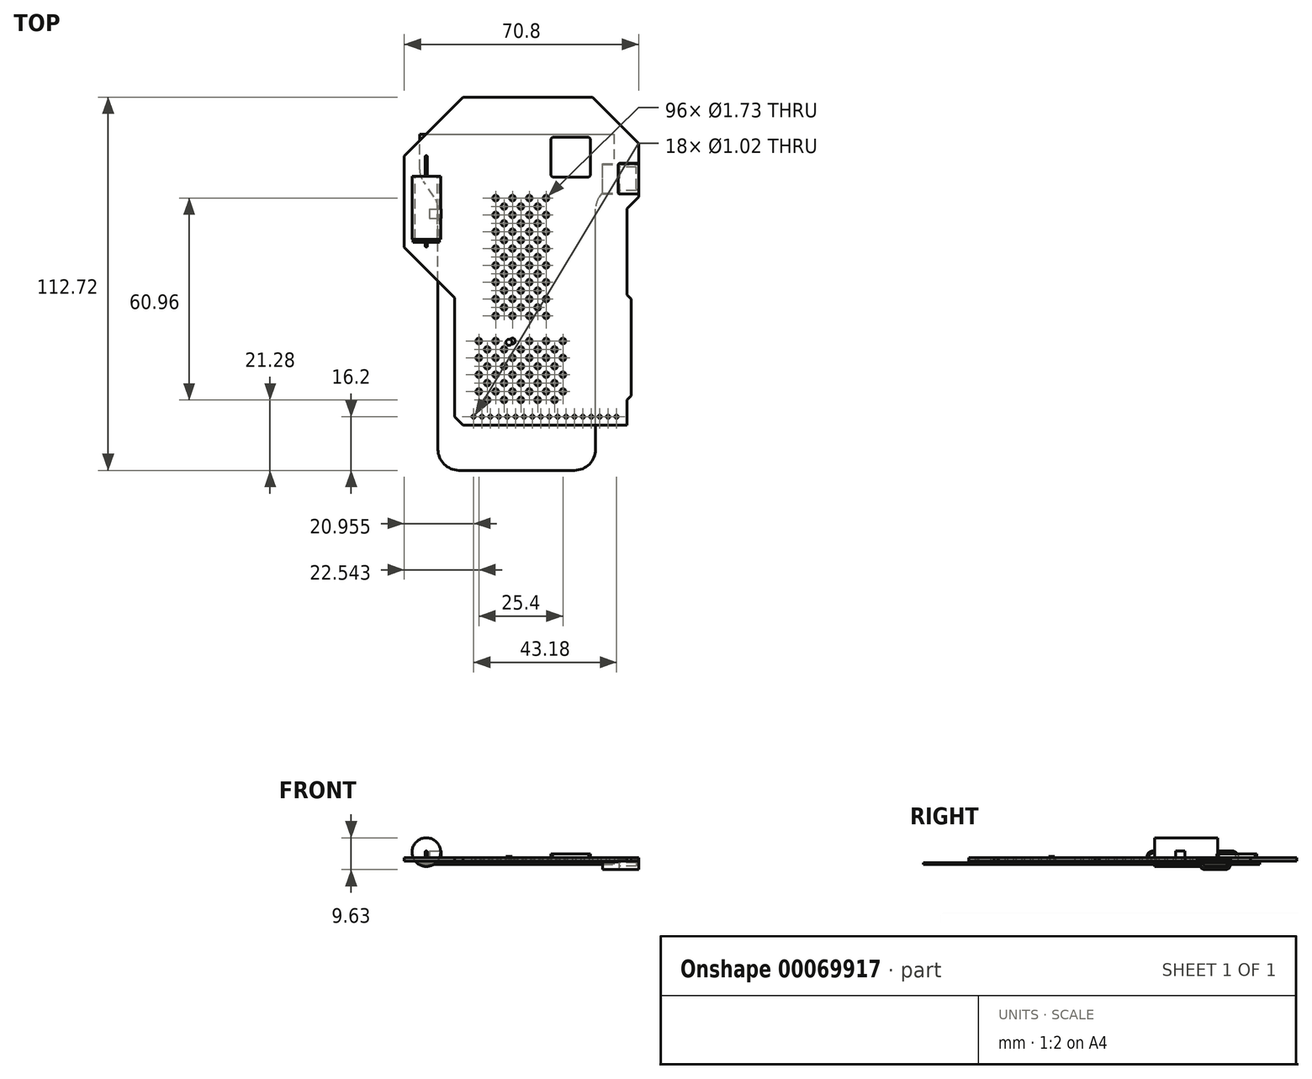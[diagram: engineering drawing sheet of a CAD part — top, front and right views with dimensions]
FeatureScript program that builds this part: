
annotation { "Feature Type Name" : "Feature", "Feature Type Description" : "" }
export const myFeature = defineFeature(function(context is Context, id is Id, definition is map)
    precondition{}
    {
        {
            var Q0;
            Q0=qCreatedBy(makeId("Top.planeOp"),FACE);
            var sketch = newSketch(context, id + "F0", { "sketchPlane" : qUnion([Q0])});
            skLineSegment(sketch, "E0", {"start": v(0, 0) * mm, "end": v(-2.54, 2.54) * mm});
            skLineSegment(sketch, "E1", {"start": v(-2.54, 2.54) * mm, "end": v(-2.54, 38.42) * mm});
            skLineSegment(sketch, "E2", {"start": v(-2.54, 38.42) * mm, "end": v(-17.78, 53.66) * mm});
            skLineSegment(sketch, "E3", {"start": v(-17.78, 53.66) * mm, "end": v(-17.78, 81.28) * mm});
            skLineSegment(sketch, "E4", {"start": v(-17.78, 81.28) * mm, "end": v(0, 99.06) * mm});
            skLineSegment(sketch, "E5", {"start": v(49.53, 39.37) * mm, "end": v(50.8, 38.1) * mm});
            skLineSegment(sketch, "E6", {"start": v(50.8, 38.1) * mm, "end": v(50.8, 8.9) * mm});
            skLineSegment(sketch, "E7", {"start": v(50.8, 8.89) * mm, "end": v(49.53, 7.62) * mm});
            skLineSegment(sketch, "E8", {"start": v(49.53, 7.62) * mm, "end": v(49.53, 0) * mm});
            skLineSegment(sketch, "E9", {"start": v(49.53, 0) * mm, "end": v(0, 0) * mm});
            skLineSegment(sketch, "E10.trimOffspring", {"start": v(0, 99.06) * mm, "end": v(39.05, 99.06) * mm});
            skLineSegment(sketch, "E11", {"start": v(53.02, 79.06) * mm, "end": v(47.33, 79.06) * mm});
            skLineSegment(sketch, "E12", {"start": v(46.82, 78.56) * mm, "end": v(46.82, 70.31) * mm});
            skLineSegment(sketch, "E13", {"start": v(47.33, 69.81) * mm, "end": v(53.02, 69.81) * mm});
            skLineSegment(sketch, "E14.trimOffspring", {"start": v(53.02, 69.81) * mm, "end": v(53.02, 68.9) * mm});
            skArc(sketch, "E15", {"start": v(47.33, 79.06) * mm, "mid": v(46.97, 78.91) * mm, "end": v(46.82, 78.56) * mm});
            skArc(sketch, "E16", {"start": v(46.82, 70.31) * mm, "mid": v(46.97, 69.96) * mm, "end": v(47.33, 69.81) * mm});
            skLineSegment(sketch, "E17.bottom", {"start": v(-15.56, 75.18) * mm, "end": v(-6.67, 75.18) * mm});
            skLineSegment(sketch, "E17.top", {"start": v(-15.56, 55.24) * mm, "end": v(-6.67, 55.24) * mm});
            skLineSegment(sketch, "E17.left", {"start": v(-15.56, 75.18) * mm, "end": v(-15.56, 55.24) * mm});
            skLineSegment(sketch, "E17.right", {"start": v(-6.67, 75.18) * mm, "end": v(-6.67, 55.24) * mm});
            skLineSegment(sketch, "E18", {"start": v(53.02, 68.9) * mm, "end": v(49.53, 65.4) * mm});
            skLineSegment(sketch, "E19", {"start": v(53.02, 85.1) * mm, "end": v(53.02, 85.1) * mm});
            skLineSegment(sketch, "E20", {"start": v(53.02, 85.1) * mm, "end": v(53.02, 79.06) * mm});
            skLineSegment(sketch, "E21", {"start": v(49.53, 65.4) * mm, "end": v(49.53, 39.37) * mm});
            skLineSegment(sketch, "E22", {"start": v(53.02, 85.1) * mm, "end": v(39.05, 99.06) * mm});
            skSolve(sketch);
        }
        {
            var Q0;
            Q0=makeQuery(id+"F0.imprint","IMPRINT",FACE,{"disambiguationData":[TD([[makeQuery(id+"F0.imprint","IMPRINT",EDGE,{"derivedFrom":sQuery(id+"F0.wireOp",EDGE,"E0")}),-1.0]])]});
            extrude(context, id + "F1", {"entities" : qUnion([Q0]), "depth" : 1 * mm});
        }
        {
            var Q0;
            Q0=makeQuery(id+"F1.opExtrude","CAP_FACE",FACE,{"disambiguationData":[OSD([sQuery(id+"F0.wireOp",EDGE,"E0"),sQuery(id+"F0.wireOp",EDGE,"E1"),sQuery(id+"F0.wireOp",EDGE,"E2"),sQuery(id+"F0.wireOp",EDGE,"E3"),sQuery(id+"F0.wireOp",EDGE,"E4"),sQuery(id+"F0.wireOp",EDGE,"5DMx5BRq-zjiZ-Dy7R-1o2c-MqwjRMZUTAln"),sQuery(id+"F0.wireOp",EDGE,"E5"),sQuery(id+"F0.wireOp",EDGE,"E6"),sQuery(id+"F0.wireOp",EDGE,"E7"),sQuery(id+"F0.wireOp",EDGE,"E8"),sQuery(id+"F0.wireOp",EDGE,"E9"),sQuery(id+"F0.wireOp",EDGE,"E10.trimOffspring"),sQuery(id+"F0.wireOp",EDGE,"E11"),sQuery(id+"F0.wireOp",EDGE,"E12"),sQuery(id+"F0.wireOp",EDGE,"E13"),sQuery(id+"F0.wireOp",EDGE,"E14.trimOffspring"),sQuery(id+"F0.wireOp",EDGE,"E15"),sQuery(id+"F0.wireOp",EDGE,"E16"),sQuery(id+"F0.wireOp",EDGE,"E17.bottom"),sQuery(id+"F0.wireOp",EDGE,"E17.top"),sQuery(id+"F0.wireOp",EDGE,"E17.left"),sQuery(id+"F0.wireOp",EDGE,"E17.right")])],"isStart":false});
            var sketch = newSketch(context, id + "F2", { "sketchPlane" : qUnion([Q0])});
            skCircle(sketch, "E23", {"center": v(17.46, 50.8) * mm, "radius": 0.86 * mm});
            skLineSegment(sketch, "E24", {"start": v(12.38, 50.8) * mm, "end": v(22.54, 50.8) * mm, "construction": true});
            skCircle(sketch, "E25", {"center": v(22.54, 50.8) * mm, "radius": 0.86 * mm});
            skCircle(sketch, "E26", {"center": v(12.38, 50.8) * mm, "radius": 0.86 * mm});
            skLineSegment(sketch, "E27", {"start": v(9.84, 53.34) * mm, "end": v(25.08, 53.34) * mm, "construction": true});
            skCircle(sketch, "E28", {"center": v(9.84, 53.34) * mm, "radius": 0.86 * mm});
            skCircle(sketch, "E29", {"center": v(14.92, 53.34) * mm, "radius": 0.86 * mm});
            skCircle(sketch, "E30", {"center": v(20, 53.34) * mm, "radius": 0.86 * mm});
            skCircle(sketch, "E31", {"center": v(25.08, 53.34) * mm, "radius": 0.86 * mm});
            skLineSegment(sketch, "E32", {"start": v(17.46, 50.8) * mm, "end": v(17.46, 53.34) * mm, "construction": true});
            skCircle(sketch, "E33.1.0.0", {"center": v(12.38, 55.88) * mm, "radius": 0.86 * mm});
            skCircle(sketch, "E33.1.0.1", {"center": v(9.84, 58.42) * mm, "radius": 0.86 * mm});
            skCircle(sketch, "E33.1.0.2", {"center": v(14.92, 58.42) * mm, "radius": 0.86 * mm});
            skCircle(sketch, "E33.1.0.3", {"center": v(17.46, 55.88) * mm, "radius": 0.86 * mm});
            skCircle(sketch, "E33.1.0.4", {"center": v(20, 58.42) * mm, "radius": 0.86 * mm});
            skCircle(sketch, "E33.1.0.5", {"center": v(22.54, 55.88) * mm, "radius": 0.86 * mm});
            skCircle(sketch, "E33.1.0.6", {"center": v(25.08, 58.42) * mm, "radius": 0.86 * mm});
            skCircle(sketch, "E33.2.0.0", {"center": v(12.38, 60.96) * mm, "radius": 0.86 * mm});
            skCircle(sketch, "E33.2.0.1", {"center": v(9.84, 63.5) * mm, "radius": 0.86 * mm});
            skCircle(sketch, "E33.2.0.2", {"center": v(14.92, 63.5) * mm, "radius": 0.86 * mm});
            skCircle(sketch, "E33.2.0.3", {"center": v(17.46, 60.96) * mm, "radius": 0.86 * mm});
            skCircle(sketch, "E33.2.0.4", {"center": v(20, 63.5) * mm, "radius": 0.86 * mm});
            skCircle(sketch, "E33.2.0.5", {"center": v(22.54, 60.96) * mm, "radius": 0.86 * mm});
            skCircle(sketch, "E33.2.0.6", {"center": v(25.08, 63.5) * mm, "radius": 0.86 * mm});
            skLineSegment(sketch, "E33.direction1", {"start": v(12.38, 50.8) * mm, "end": v(12.38, 55.88) * mm, "construction": true});
            skCircle(sketch, "E34.0.3.0", {"center": v(12.38, 66.04) * mm, "radius": 0.86 * mm});
            skCircle(sketch, "E34.2.3.0", {"center": v(9.84, 68.58) * mm, "radius": 0.86 * mm});
            skCircle(sketch, "E34.4.3.0", {"center": v(14.92, 68.58) * mm, "radius": 0.86 * mm});
            skCircle(sketch, "E34.6.3.0", {"center": v(17.46, 66.04) * mm, "radius": 0.86 * mm});
            skCircle(sketch, "E34.8.3.0", {"center": v(20, 68.58) * mm, "radius": 0.86 * mm});
            skCircle(sketch, "E34.10.3.0", {"center": v(22.54, 66.04) * mm, "radius": 0.86 * mm});
            skCircle(sketch, "E34.12.3.0", {"center": v(25.08, 68.58) * mm, "radius": 0.86 * mm});
            skCircle(sketch, "E35.1.0.0", {"center": v(9.84, 48.26) * mm, "radius": 0.86 * mm});
            skCircle(sketch, "E35.1.0.1", {"center": v(12.38, 45.72) * mm, "radius": 0.86 * mm});
            skCircle(sketch, "E35.1.0.2", {"center": v(14.92, 48.26) * mm, "radius": 0.86 * mm});
            skCircle(sketch, "E35.1.0.3", {"center": v(17.46, 45.72) * mm, "radius": 0.86 * mm});
            skCircle(sketch, "E35.1.0.4", {"center": v(20, 48.26) * mm, "radius": 0.86 * mm});
            skCircle(sketch, "E35.1.0.5", {"center": v(22.54, 45.72) * mm, "radius": 0.86 * mm});
            skCircle(sketch, "E35.1.0.6", {"center": v(25.08, 48.26) * mm, "radius": 0.86 * mm});
            skCircle(sketch, "E35.2.0.0", {"center": v(9.84, 43.18) * mm, "radius": 0.86 * mm});
            skCircle(sketch, "E35.2.0.1", {"center": v(12.38, 40.64) * mm, "radius": 0.86 * mm});
            skCircle(sketch, "E35.2.0.2", {"center": v(14.92, 43.18) * mm, "radius": 0.86 * mm});
            skCircle(sketch, "E35.2.0.3", {"center": v(17.46, 40.64) * mm, "radius": 0.86 * mm});
            skCircle(sketch, "E35.2.0.4", {"center": v(20, 43.18) * mm, "radius": 0.86 * mm});
            skCircle(sketch, "E35.2.0.5", {"center": v(22.54, 40.64) * mm, "radius": 0.86 * mm});
            skCircle(sketch, "E35.2.0.6", {"center": v(25.08, 43.18) * mm, "radius": 0.86 * mm});
            skLineSegment(sketch, "E35.direction1", {"start": v(9.84, 53.34) * mm, "end": v(9.84, 48.26) * mm, "construction": true});
            skCircle(sketch, "E36.0.3.0", {"center": v(9.84, 38.1) * mm, "radius": 0.86 * mm});
            skCircle(sketch, "E36.2.3.0", {"center": v(12.38, 35.56) * mm, "radius": 0.86 * mm});
            skCircle(sketch, "E36.4.3.0", {"center": v(14.92, 38.1) * mm, "radius": 0.86 * mm});
            skCircle(sketch, "E36.6.3.0", {"center": v(17.46, 35.56) * mm, "radius": 0.86 * mm});
            skCircle(sketch, "E36.8.3.0", {"center": v(20, 38.1) * mm, "radius": 0.86 * mm});
            skCircle(sketch, "E36.10.3.0", {"center": v(22.54, 35.56) * mm, "radius": 0.86 * mm});
            skCircle(sketch, "E36.12.3.0", {"center": v(25.08, 38.1) * mm, "radius": 0.86 * mm});
            skCircle(sketch, "E37.1.0.0", {"center": v(9.84, 33.02) * mm, "radius": 0.86 * mm});
            skCircle(sketch, "E37.1.0.1", {"center": v(14.92, 33.02) * mm, "radius": 0.86 * mm});
            skCircle(sketch, "E37.1.0.2", {"center": v(20, 33.02) * mm, "radius": 0.86 * mm});
            skCircle(sketch, "E37.1.0.3", {"center": v(25.08, 33.02) * mm, "radius": 0.86 * mm});
            skLineSegment(sketch, "E37.direction1", {"start": v(9.84, 38.1) * mm, "end": v(9.84, 33.02) * mm, "construction": true});
            skLineSegment(sketch, "E38", {"start": v(4.76, 25.4) * mm, "end": v(30.16, 25.4) * mm, "construction": true});
            skLineSegment(sketch, "E39", {"start": v(7.3, 22.86) * mm, "end": v(27.62, 22.86) * mm, "construction": true});
            skLineSegment(sketch, "E40", {"start": v(17.46, 50.8) * mm, "end": v(17.46, 25.4) * mm, "construction": true});
            skLineSegment(sketch, "E41", {"start": v(17.46, 25.4) * mm, "end": v(17.46, 22.86) * mm, "construction": true});
            skCircle(sketch, "E42", {"center": v(4.76, 25.4) * mm, "radius": 0.86 * mm});
            skCircle(sketch, "E43", {"center": v(9.84, 25.4) * mm, "radius": 0.86 * mm});
            skCircle(sketch, "E44", {"center": v(14.92, 25.4) * mm, "radius": 0.86 * mm});
            skCircle(sketch, "E45", {"center": v(20, 25.4) * mm, "radius": 0.86 * mm});
            skCircle(sketch, "E46", {"center": v(25.08, 25.4) * mm, "radius": 0.86 * mm});
            skCircle(sketch, "E47", {"center": v(30.16, 25.4) * mm, "radius": 0.86 * mm});
            skCircle(sketch, "E48", {"center": v(7.3, 22.86) * mm, "radius": 0.86 * mm});
            skCircle(sketch, "E49", {"center": v(12.38, 22.86) * mm, "radius": 0.86 * mm});
            skCircle(sketch, "E50", {"center": v(17.46, 22.86) * mm, "radius": 0.86 * mm});
            skCircle(sketch, "E51", {"center": v(22.54, 22.86) * mm, "radius": 0.86 * mm});
            skCircle(sketch, "E52", {"center": v(27.62, 22.86) * mm, "radius": 0.86 * mm});
            skCircle(sketch, "E53.1.0.0", {"center": v(4.76, 20.32) * mm, "radius": 0.86 * mm});
            skCircle(sketch, "E53.1.0.1", {"center": v(9.84, 20.32) * mm, "radius": 0.86 * mm});
            skCircle(sketch, "E53.1.0.2", {"center": v(14.92, 20.32) * mm, "radius": 0.86 * mm});
            skCircle(sketch, "E53.1.0.3", {"center": v(20, 20.32) * mm, "radius": 0.86 * mm});
            skCircle(sketch, "E53.1.0.4", {"center": v(25.08, 20.32) * mm, "radius": 0.86 * mm});
            skCircle(sketch, "E53.1.0.5", {"center": v(30.16, 20.32) * mm, "radius": 0.86 * mm});
            skCircle(sketch, "E53.1.0.6", {"center": v(27.62, 17.78) * mm, "radius": 0.86 * mm});
            skCircle(sketch, "E53.1.0.7", {"center": v(22.54, 17.78) * mm, "radius": 0.86 * mm});
            skCircle(sketch, "E53.1.0.8", {"center": v(17.46, 17.78) * mm, "radius": 0.86 * mm});
            skCircle(sketch, "E53.1.0.9", {"center": v(12.38, 17.78) * mm, "radius": 0.86 * mm});
            skCircle(sketch, "E53.1.0.10", {"center": v(7.3, 17.78) * mm, "radius": 0.86 * mm});
            skCircle(sketch, "E53.2.0.0", {"center": v(4.76, 15.24) * mm, "radius": 0.86 * mm});
            skCircle(sketch, "E53.2.0.1", {"center": v(9.84, 15.24) * mm, "radius": 0.86 * mm});
            skCircle(sketch, "E53.2.0.2", {"center": v(14.92, 15.24) * mm, "radius": 0.86 * mm});
            skCircle(sketch, "E53.2.0.3", {"center": v(20, 15.24) * mm, "radius": 0.86 * mm});
            skCircle(sketch, "E53.2.0.4", {"center": v(25.08, 15.24) * mm, "radius": 0.86 * mm});
            skCircle(sketch, "E53.2.0.5", {"center": v(30.16, 15.24) * mm, "radius": 0.86 * mm});
            skCircle(sketch, "E53.2.0.6", {"center": v(27.62, 12.7) * mm, "radius": 0.86 * mm});
            skCircle(sketch, "E53.2.0.7", {"center": v(22.54, 12.7) * mm, "radius": 0.86 * mm});
            skCircle(sketch, "E53.2.0.8", {"center": v(17.46, 12.7) * mm, "radius": 0.86 * mm});
            skCircle(sketch, "E53.2.0.9", {"center": v(12.38, 12.7) * mm, "radius": 0.86 * mm});
            skCircle(sketch, "E53.2.0.10", {"center": v(7.3, 12.7) * mm, "radius": 0.86 * mm});
            skLineSegment(sketch, "E53.direction1", {"start": v(4.76, 25.4) * mm, "end": v(4.76, 20.32) * mm, "construction": true});
            skCircle(sketch, "E54.0.3.0", {"center": v(4.76, 10.16) * mm, "radius": 0.86 * mm});
            skCircle(sketch, "E54.2.3.0", {"center": v(9.84, 10.16) * mm, "radius": 0.86 * mm});
            skCircle(sketch, "E54.4.3.0", {"center": v(14.92, 10.16) * mm, "radius": 0.86 * mm});
            skCircle(sketch, "E54.6.3.0", {"center": v(20, 10.16) * mm, "radius": 0.86 * mm});
            skCircle(sketch, "E54.8.3.0", {"center": v(25.08, 10.16) * mm, "radius": 0.86 * mm});
            skCircle(sketch, "E54.10.3.0", {"center": v(30.16, 10.16) * mm, "radius": 0.86 * mm});
            skCircle(sketch, "E54.12.3.0", {"center": v(27.62, 7.62) * mm, "radius": 0.86 * mm});
            skCircle(sketch, "E54.14.3.0", {"center": v(22.54, 7.62) * mm, "radius": 0.86 * mm});
            skCircle(sketch, "E54.16.3.0", {"center": v(17.46, 7.62) * mm, "radius": 0.86 * mm});
            skCircle(sketch, "E54.18.3.0", {"center": v(12.38, 7.62) * mm, "radius": 0.86 * mm});
            skCircle(sketch, "E54.20.3.0", {"center": v(7.3, 7.62) * mm, "radius": 0.86 * mm});
            skCircle(sketch, "E55", {"center": v(3.17, 2.54) * mm, "radius": 0.5 * mm});
            skCircle(sketch, "E56.1.0.0", {"center": v(5.72, 2.54) * mm, "radius": 0.5 * mm});
            skCircle(sketch, "E56.2.0.0", {"center": v(8.26, 2.54) * mm, "radius": 0.5 * mm});
            skCircle(sketch, "E56.3.0.0", {"center": v(10.8, 2.54) * mm, "radius": 0.5 * mm});
            skCircle(sketch, "E56.4.0.0", {"center": v(13.33, 2.54) * mm, "radius": 0.5 * mm});
            skCircle(sketch, "E56.5.0.0", {"center": v(15.88, 2.54) * mm, "radius": 0.5 * mm});
            skCircle(sketch, "E56.6.0.0", {"center": v(18.41, 2.54) * mm, "radius": 0.5 * mm});
            skCircle(sketch, "E56.7.0.0", {"center": v(20.96, 2.54) * mm, "radius": 0.5 * mm});
            skCircle(sketch, "E56.8.0.0", {"center": v(23.5, 2.54) * mm, "radius": 0.5 * mm});
            skCircle(sketch, "E56.9.0.0", {"center": v(26.04, 2.54) * mm, "radius": 0.5 * mm});
            skCircle(sketch, "E56.10.0.0", {"center": v(28.58, 2.54) * mm, "radius": 0.5 * mm});
            skCircle(sketch, "E56.11.0.0", {"center": v(31.12, 2.54) * mm, "radius": 0.5 * mm});
            skCircle(sketch, "E56.12.0.0", {"center": v(33.65, 2.54) * mm, "radius": 0.5 * mm});
            skCircle(sketch, "E56.13.0.0", {"center": v(36.2, 2.54) * mm, "radius": 0.5 * mm});
            skCircle(sketch, "E56.14.0.0", {"center": v(38.73, 2.54) * mm, "radius": 0.5 * mm});
            skCircle(sketch, "E56.15.0.0", {"center": v(41.27, 2.54) * mm, "radius": 0.5 * mm});
            skCircle(sketch, "E56.16.0.0", {"center": v(43.81, 2.54) * mm, "radius": 0.5 * mm});
            skCircle(sketch, "E56.17.0.0", {"center": v(46.35, 2.54) * mm, "radius": 0.5 * mm});
            skLineSegment(sketch, "E56.direction1", {"start": v(3.17, 2.54) * mm, "end": v(5.72, 2.54) * mm, "construction": true});
            skSolve(sketch);
        }
        {
            var Q0;
            Q0 = qSketchRegion(id + "F2", true);
            extrude(context, id + "F3", {"entities" : qUnion([Q0]), "operationType" : NewBodyOperationType.REMOVE, "endBound" : BoundingType.THROUGH_ALL, "oppositeDirection" : true, "depth" : 25.4 * mm});
        }
        {
            var Q0;
            Q0=makeQuery(id+"F1.opExtrude","CAP_FACE",FACE,{"disambiguationData":[OSD([sQuery(id+"F0.wireOp",EDGE,"E0"),sQuery(id+"F0.wireOp",EDGE,"E1"),sQuery(id+"F0.wireOp",EDGE,"E2"),sQuery(id+"F0.wireOp",EDGE,"E3"),sQuery(id+"F0.wireOp",EDGE,"E4"),sQuery(id+"F0.wireOp",EDGE,"wfJOyMOF-7hrh-DqS5-em1k-46T7LlYXctm8"),sQuery(id+"F0.wireOp",EDGE,"5DMx5BRq-zjiZ-Dy7R-1o2c-MqwjRMZUTAln"),sQuery(id+"F0.wireOp",EDGE,"E5"),sQuery(id+"F0.wireOp",EDGE,"E6"),sQuery(id+"F0.wireOp",EDGE,"E7"),sQuery(id+"F0.wireOp",EDGE,"E8"),sQuery(id+"F0.wireOp",EDGE,"E9")])],"isStart":false});
            var sketch = newSketch(context, id + "F4", { "sketchPlane" : qUnion([Q0])});
            skCircle(sketch, "E57", {"center": v(13.87, 25.02) * mm, "radius": 0.91 * mm});
            skSolve(sketch);
        }
        {
            var Q0;
            Q0 = qSketchRegion(id + "F4", true);
            extrude(context, id + "F5", {"entities" : qUnion([Q0]), "depth" : 0.4 * mm});
        }
        {
            var Q0;
            Q0=makeQuery(id+"F5.opExtrude","CAP_FACE",FACE,{"disambiguationData":[OSD([sQuery(id+"F4.wireOp",EDGE,"E57")])],"isStart":true});
            var sketch = newSketch(context, id + "F6", { "sketchPlane" : qUnion([Q0])});
            skCircle(sketch, "E58", {"center": v(13.87, -25.02) * mm, "radius": 0.81 * mm});
            skSolve(sketch);
        }
        {
            var Q0;
            Q0=makeQuery(id+"F6.imprint","IMPRINT",FACE,{"disambiguationData":[TD([[makeQuery(id+"F6.imprint","IMPRINT",EDGE,{"derivedFrom":sQuery(id+"F6.wireOp",EDGE,"E58")}),1.0]])]});
            extrude(context, id + "F7", {"entities" : qUnion([Q0]), "operationType" : NewBodyOperationType.ADD, "depth" : 1.52 * mm});
        }
        {
            var Q0;
            Q0=makeQuery(id+"F7.opExtrude","CAP_FACE",FACE,{"disambiguationData":[OSD([sQuery(id+"F6.wireOp",EDGE,"E58")])],"isStart":false});
            var sketch = newSketch(context, id + "F8", { "sketchPlane" : qUnion([Q0])});
            skLineSegment(sketch, "E59.bottom", {"start": v(33.68, 13.66) * mm, "end": v(-1.25, 13.66) * mm});
            skLineSegment(sketch, "E59.left", {"start": v(40.03, 7.31) * mm, "end": v(40.03, -65.3) * mm});
            skLineSegment(sketch, "E59.right", {"start": v(-7.6, 7.31) * mm, "end": v(-7.6, -65.3) * mm});
            skPoint(sketch, "E60.visualSharp", {"position": v(-7.6, 13.66) * mm});
            skArc(sketch, "E60.filletArc", {"start": v(-1.25, 13.66) * mm, "mid": v(-5.74, 11.8) * mm, "end": v(-7.6, 7.31) * mm});
            skPoint(sketch, "E61.visualSharp", {"position": v(40.03, 13.66) * mm});
            skArc(sketch, "E61.filletArc", {"start": v(40.03, 7.31) * mm, "mid": v(38.17, 11.8) * mm, "end": v(33.68, 13.66) * mm});
            skLineSegment(sketch, "E62", {"start": v(-8.74, -68.94) * mm, "end": v(-12, -73.6) * mm});
            skLineSegment(sketch, "E63", {"start": v(-13.15, -77.24) * mm, "end": v(-13.15, -87.94) * mm});
            skLineSegment(sketch, "E64", {"start": v(-13.15, -87.94) * mm, "end": v(45.58, -87.94) * mm});
            skLineSegment(sketch, "E65", {"start": v(45.58, -87.94) * mm, "end": v(45.58, -77.24) * mm});
            skLineSegment(sketch, "E66", {"start": v(44.44, -73.6) * mm, "end": v(41.18, -68.94) * mm});
            skLineSegment(sketch, "E67", {"start": v(-13.15, -75.24) * mm, "end": v(45.58, -75.24) * mm, "construction": true});
            skLineSegment(sketch, "E68", {"start": v(40.03, -67.3) * mm, "end": v(-7.6, -67.3) * mm, "construction": true});
            skPoint(sketch, "E69.visualSharp", {"position": v(-13.15, -75.24) * mm});
            skArc(sketch, "E69.filletArc", {"start": v(-12, -73.6) * mm, "mid": v(-12.86, -75.33) * mm, "end": v(-13.15, -77.24) * mm});
            skPoint(sketch, "E70.visualSharp", {"position": v(45.58, -75.24) * mm});
            skArc(sketch, "E70.filletArc", {"start": v(45.58, -77.24) * mm, "mid": v(45.3, -75.33) * mm, "end": v(44.44, -73.6) * mm});
            skPoint(sketch, "E71.visualSharp", {"position": v(40.03, -67.3) * mm});
            skArc(sketch, "E71.filletArc", {"start": v(40.03, -65.3) * mm, "mid": v(40.32, -67.2) * mm, "end": v(41.18, -68.94) * mm});
            skPoint(sketch, "E72.visualSharp", {"position": v(-7.6, -67.3) * mm});
            skArc(sketch, "E72.filletArc", {"start": v(-8.74, -68.94) * mm, "mid": v(-7.9, -67.2) * mm, "end": v(-7.6, -65.3) * mm});
            skSolve(sketch);
        }
        {
            var Q0;
            Q0 = qSketchRegion(id + "F8", true);
            extrude(context, id + "F9", {"entities" : qUnion([Q0]), "depth" : .45 * mm});
        }
        {
            var Q0;
            Q0=makeQuery(id+"F1.opExtrude","SWEPT_FACE",FACE,{"disambiguationData":[OSD([sQuery(id+"F0.wireOp",EDGE,"E14.trimOffspring")])]});
            var sketch = newSketch(context, id + "F10", { "sketchPlane" : qUnion([Q0])});
            skArc(sketch, "E73", {"start": v(71.36, 0.5) * mm, "mid": v(69.84, -1.02) * mm, "end": v(71.36, -2.55) * mm});
            skLineSegment(sketch, "E74", {"start": v(71.36, 0.5) * mm, "end": v(71.36, -2.55) * mm, "construction": true});
            skArc(sketch, "E75", {"start": v(77.5, -2.55) * mm, "mid": v(79.03, -1.02) * mm, "end": v(77.5, 0.5) * mm});
            skLineSegment(sketch, "E76", {"start": v(77.5, 0.5) * mm, "end": v(77.5, -2.55) * mm, "construction": true});
            skLineSegment(sketch, "E77", {"start": v(71.36, 0.5) * mm, "end": v(77.5, 0.5) * mm});
            skLineSegment(sketch, "E78", {"start": v(77.5, -2.55) * mm, "end": v(71.36, -2.55) * mm});
            skLineSegment(sketch, "E79", {"start": v(69.84, -1.02) * mm, "end": v(79.03, -1.02) * mm, "construction": true});
            skSolve(sketch);
        }
        {
            var Q0;
            Q0 = qSketchRegion(id + "F10", true);
            var Q1;
            Q1=makeQuery(id+"F1.opExtrude","SWEPT_FACE",FACE,{"disambiguationData":[OSD([sQuery(id+"F0.wireOp",EDGE,"E12")])]});
            extrude(context, id + "F11", {"entities" : qUnion([Q0]), "endBound" : BoundingType.UP_TO_SURFACE, "oppositeDirection" : true, "endBoundEntityFace" : qUnion([Q1]), "depth" : 25.4 * mm});
        }
        {
            var Q0;
            Q0=makeQuery(id+"F11.opExtrude","CAP_FACE",FACE,{"disambiguationData":[OSD([sQuery(id+"F10.wireOp",EDGE,"E73"),sQuery(id+"F10.wireOp",EDGE,"E75"),sQuery(id+"F10.wireOp",EDGE,"E77"),sQuery(id+"F10.wireOp",EDGE,"E78")])],"isStart":true});
            var sketch = newSketch(context, id + "F12", { "sketchPlane" : qUnion([Q0])});
            skArc(sketch, "E80.0", {"start": v(77.5, -2.3) * mm, "mid": v(78.78, -1.02) * mm, "end": v(77.5, 0.25) * mm});
            skLineSegment(sketch, "E80.1", {"start": v(77.5, -2.3) * mm, "end": v(71.36, -2.3) * mm});
            skArc(sketch, "E80.2", {"start": v(71.36, 0.25) * mm, "mid": v(70.1, -1.02) * mm, "end": v(71.36, -2.3) * mm});
            skLineSegment(sketch, "E80.3", {"start": v(71.36, 0.25) * mm, "end": v(77.5, 0.25) * mm});
            skSolve(sketch);
        }
        {
            var Q0;
            Q0=makeQuery(id+"F12.imprint","IMPRINT",FACE,{"disambiguationData":[TD([[makeQuery(id+"F12.imprint","IMPRINT",EDGE,{"derivedFrom":sQuery(id+"F12.wireOp",EDGE,"E80.0")}),1.0]])]});
            extrude(context, id + "F13", {"entities" : qUnion([Q0]), "operationType" : NewBodyOperationType.REMOVE, "oppositeDirection" : true, "depth" : 5.84 * mm});
        }
        {
            var Q0;
            Q0=makeQuery(id+"F13.boolean.opBoolean","COPY",FACE,{"derivedFrom":makeQuery(id+"F13.opExtrude","CAP_FACE",FACE,{"disambiguationData":[OSD([sQuery(id+"F12.wireOp",EDGE,"E80.0"),sQuery(id+"F12.wireOp",EDGE,"E80.1"),sQuery(id+"F12.wireOp",EDGE,"E80.2"),sQuery(id+"F12.wireOp",EDGE,"E80.3")])],"isStart":false})});
            var sketch = newSketch(context, id + "F14", { "sketchPlane" : qUnion([Q0])});
            skArc(sketch, "E81.0", {"start": v(71.36, -0.52) * mm, "mid": v(70.85, -1.02) * mm, "end": v(71.36, -1.53) * mm});
            skLineSegment(sketch, "E81.1", {"start": v(71.36, -0.52) * mm, "end": v(77.5, -0.52) * mm});
            skArc(sketch, "E81.2", {"start": v(77.5, -1.53) * mm, "mid": v(78.02, -1.02) * mm, "end": v(77.5, -0.52) * mm});
            skLineSegment(sketch, "E81.3", {"start": v(77.5, -1.53) * mm, "end": v(71.36, -1.53) * mm});
            skSolve(sketch);
        }
        {
            var Q0;
            Q0=makeQuery(id+"F14.imprint","IMPRINT",FACE,{"disambiguationData":[TD([[makeQuery(id+"F14.imprint","IMPRINT",EDGE,{"derivedFrom":sQuery(id+"F14.wireOp",EDGE,"E81.0")}),1.0]])]});
            extrude(context, id + "F15", {"entities" : qUnion([Q0]), "operationType" : NewBodyOperationType.ADD, "depth" : 5.08 * mm});
        }
        {
            var Q0;
            Q0=makeQuery(id+"F1.opExtrude","SWEPT_FACE",FACE,{"disambiguationData":[OSD([sQuery(id+"F0.wireOp",EDGE,"E17.bottom")])]});
            var sketch = newSketch(context, id + "F16", { "sketchPlane" : qUnion([Q0])});
            skCircle(sketch, "E82", {"center": v(-11.11, 2.75) * mm, "radius": 4.33 * mm});
            skLineSegment(sketch, "E83", {"start": v(-15.56, 1) * mm, "end": v(-6.67, 1) * mm, "construction": true});
            skLineSegment(sketch, "E84", {"start": v(-11.11, 1) * mm, "end": v(-11.11, 2.75) * mm, "construction": true});
            skSolve(sketch);
        }
        {
            var Q0;
            Q0 = qSketchRegion(id + "F16", true);
            extrude(context, id + "F17", {"entities" : qUnion([Q0]), "depth" : 19.05 * mm});
        }
        {
            var Q0;
            Q0=makeQuery(id+"F1.opExtrude","SWEPT_FACE",FACE,{"disambiguationData":[OSD([sQuery(id+"F0.wireOp",EDGE,"E17.left")])]});
            var Q1;
            Q1=makeQuery(id+"F1.opExtrude","SWEPT_FACE",FACE,{"disambiguationData":[OSD([sQuery(id+"F0.wireOp",EDGE,"E17.right")])]});
            cPlane(context, id + "F18", {"entities" : qUnion([Q0, Q1]), "cplaneType" : CPlaneType.MID_PLANE, "offset" : 152.4 * mm, "width" : 152.4 * mm, "height" : 152.4 * mm});
        }
        {
            var Q0;
            Q0=qCreatedBy(id+"F18.planeOp",FACE);
            var sketch = newSketch(context, id + "F19", { "sketchPlane" : qUnion([Q0])});
            skLineSegment(sketch, "E85", {"start": v(75.18, 2.75) * mm, "end": v(79.55, 2.75) * mm});
            skLineSegment(sketch, "E86", {"start": v(75.18, 7.08) * mm, "end": v(75.18, -1.58) * mm, "construction": true});
            skArc(sketch, "E87", {"start": v(81.08, 1.22) * mm, "mid": v(80.63, 2.3) * mm, "end": v(79.55, 2.75) * mm});
            skLineSegment(sketch, "E88", {"start": v(79.55, 2.75) * mm, "end": v(79.55, 1) * mm, "construction": true});
            skLineSegment(sketch, "E89", {"start": v(81.08, 1.22) * mm, "end": v(81.08, 1) * mm});
            skLineSegment(sketch, "E90", {"start": v(79.55, 1) * mm, "end": v(81.08, 1) * mm, "construction": true});
            skLineSegment(sketch, "E91", {"start": v(56.13, 7.08) * mm, "end": v(56.13, -1.58) * mm, "construction": true});
            skLineSegment(sketch, "E92", {"start": v(56.13, 2.75) * mm, "end": v(55.63, 2.75) * mm});
            skArc(sketch, "E93", {"start": v(55.63, 2.75) * mm, "mid": v(54.55, 2.3) * mm, "end": v(54.1, 1.22) * mm});
            skLineSegment(sketch, "E94", {"start": v(54.1, 1.22) * mm, "end": v(54.1, 1) * mm});
            skLineSegment(sketch, "E95", {"start": v(75.18, 2.75) * mm, "end": v(56.13, 2.75) * mm});
            skSolve(sketch);
        }
        {
            var Q0;
            Q0=makeQuery(id+"F17.opExtrude","CAP_FACE",FACE,{"disambiguationData":[OSD([sQuery(id+"F16.wireOp",EDGE,"E82")])],"isStart":true});
            var sketch = newSketch(context, id + "F20", { "sketchPlane" : qUnion([Q0])});
            skCircle(sketch, "E96", {"center": v(11.11, 2.75) * mm, "radius": 0.32 * mm});
            skSolve(sketch);
        }
        {
            var Q0;
            Q0=makeQuery(id+"F20.imprint","IMPRINT",FACE,{"disambiguationData":[TD([[makeQuery(id+"F20.imprint","IMPRINT",EDGE,{"derivedFrom":sQuery(id+"F20.wireOp",EDGE,"E96")}),1.0]])]});
            var Q1;
            Q1=sQuery(id+"F19.wireOp",EDGE,"E89");
            var Q2;
            Q2=sQuery(id+"F19.wireOp",EDGE,"E87");
            var Q3;
            Q3=sQuery(id+"F19.wireOp",EDGE,"E85");
            sweep(context, id + "F21", {"operationType" : NewBodyOperationType.ADD, "profiles" : qUnion([Q0]), "path" : qUnion([Q1, Q2, Q3])});
        }
        {
            var Q0;
            Q0 = qSketchRegion(id + "F20", true);
            var Q1;
            Q1=sQuery(id+"F19.wireOp",EDGE,"E92");
            var Q2;
            Q2=sQuery(id+"F19.wireOp",EDGE,"E93");
            var Q3;
            Q3=sQuery(id+"F19.wireOp",EDGE,"E94");
            var Q4;
            Q4=sQuery(id+"F19.wireOp",EDGE,"E95");
            sweep(context, id + "F22", {"operationType" : NewBodyOperationType.ADD, "profiles" : qUnion([Q0]), "path" : qUnion([Q1, Q2, Q3, Q4])});
        }
        {
            var Q0;
            Q0=makeQuery(id+"F11.opExtrude","CAP_FACE",FACE,{"disambiguationData":[OSD([sQuery(id+"F10.wireOp",EDGE,"E73"),sQuery(id+"F10.wireOp",EDGE,"E75"),sQuery(id+"F10.wireOp",EDGE,"E77"),sQuery(id+"F10.wireOp",EDGE,"E78")])],"isStart":false});
            var sketch = newSketch(context, id + "F23", { "sketchPlane" : qUnion([Q0])});
            skLineSegment(sketch, "E97.0", {"start": v(-71.36, -2.55) * mm, "end": v(-77.5, -2.55) * mm});
            skArc(sketch, "E97.1", {"start": v(-71.36, -2.55) * mm, "mid": v(-70.01, -1.73) * mm, "end": v(-70.1, -0.16) * mm});
            skArc(sketch, "E97.3", {"start": v(-78.76, -0.16) * mm, "mid": v(-78.86, -1.73) * mm, "end": v(-77.5, -2.55) * mm});
            skLineSegment(sketch, "E98", {"start": v(-70.1, -0.16) * mm, "end": v(-78.76, -0.16) * mm});
            skLineSegment(sketch, "E99", {"start": v(-77.5, 0.5) * mm, "end": v(-77.5, -2.55) * mm, "construction": true});
            skSolve(sketch);
        }
        {
            var Q0;
            Q0 = qSketchRegion(id + "F23", true);
            extrude(context, id + "F24", {"entities" : qUnion([Q0]), "operationType" : NewBodyOperationType.ADD, "depth" : 4.65 * mm});
        }
        {
            var Q0;
            Q0=makeQuery(id+"F1.opExtrude","CAP_FACE",FACE,{"disambiguationData":[OSD([sQuery(id+"F0.wireOp",EDGE,"E0"),sQuery(id+"F0.wireOp",EDGE,"E1"),sQuery(id+"F0.wireOp",EDGE,"E2"),sQuery(id+"F0.wireOp",EDGE,"E3"),sQuery(id+"F0.wireOp",EDGE,"E4"),sQuery(id+"F0.wireOp",EDGE,"5DMx5BRq-zjiZ-Dy7R-1o2c-MqwjRMZUTAln"),sQuery(id+"F0.wireOp",EDGE,"E5"),sQuery(id+"F0.wireOp",EDGE,"E6"),sQuery(id+"F0.wireOp",EDGE,"E7"),sQuery(id+"F0.wireOp",EDGE,"E8"),sQuery(id+"F0.wireOp",EDGE,"E9"),sQuery(id+"F0.wireOp",EDGE,"E10.trimOffspring"),sQuery(id+"F0.wireOp",EDGE,"E11"),sQuery(id+"F0.wireOp",EDGE,"E12"),sQuery(id+"F0.wireOp",EDGE,"E13"),sQuery(id+"F0.wireOp",EDGE,"E14.trimOffspring"),sQuery(id+"F0.wireOp",EDGE,"E15"),sQuery(id+"F0.wireOp",EDGE,"E16"),sQuery(id+"F0.wireOp",EDGE,"E17.bottom"),sQuery(id+"F0.wireOp",EDGE,"E17.top"),sQuery(id+"F0.wireOp",EDGE,"E17.left"),sQuery(id+"F0.wireOp",EDGE,"E17.right"),sQuery(id+"F0.wireOp",EDGE,"E18"),sQuery(id+"F0.wireOp",EDGE,"E19"),sQuery(id+"F0.wireOp",EDGE,"E20"),sQuery(id+"F0.wireOp",EDGE,"E21")])],"isStart":false});
            var sketch = newSketch(context, id + "F25", { "sketchPlane" : qUnion([Q0])});
            skLineSegment(sketch, "E100.bottom", {"start": v(26.47, 86.94) * mm, "end": v(38.47, 86.94) * mm});
            skLineSegment(sketch, "E100.top", {"start": v(26.47, 74.94) * mm, "end": v(38.47, 74.94) * mm});
            skLineSegment(sketch, "E100.left", {"start": v(26.47, 86.94) * mm, "end": v(26.47, 74.94) * mm});
            skLineSegment(sketch, "E100.right", {"start": v(38.47, 86.94) * mm, "end": v(38.47, 74.94) * mm});
            skSolve(sketch);
        }
        {
            var Q0;
            Q0 = qSketchRegion(id + "F25", true);
            extrude(context, id + "F26", {"entities" : qUnion([Q0]), "depth" : 1.2 * mm});
        }
        {
            var Q0;
            Q0=makeQuery(id+"F26.opExtrude","SWEPT_EDGE",EDGE,{"disambiguationData":[OSD([sQuery(id+"F25.wireOp",EDGE,"E100.top"),sQuery(id+"F25.wireOp",EDGE,"E100.right")])]});
            var Q1;
            Q1=makeQuery(id+"F26.opExtrude","SWEPT_EDGE",EDGE,{"disambiguationData":[OSD([sQuery(id+"F25.wireOp",EDGE,"E100.top"),sQuery(id+"F25.wireOp",EDGE,"E100.left")])]});
            var Q2;
            Q2=makeQuery(id+"F26.opExtrude","SWEPT_EDGE",EDGE,{"disambiguationData":[OSD([sQuery(id+"F25.wireOp",EDGE,"E100.bottom"),sQuery(id+"F25.wireOp",EDGE,"E100.left")])]});
            var Q3;
            Q3=makeQuery(id+"F26.opExtrude","SWEPT_EDGE",EDGE,{"disambiguationData":[OSD([sQuery(id+"F25.wireOp",EDGE,"E100.bottom"),sQuery(id+"F25.wireOp",EDGE,"E100.right")])]});
            chamfer(context, id + "F27", {"entities" : qUnion([Q0, Q1, Q2, Q3]), "width" : 0.5 * mm, "tangentPropagation" : true});
        }
        {
            var Q0;
            Q0=makeQuery(id+"F1.opExtrude","SWEPT_FACE",FACE,{"disambiguationData":[OSD([sQuery(id+"F0.wireOp",EDGE,"E17.bottom")])]});
            var Q1;
            Q1=makeQuery(id+"F1.opExtrude","SWEPT_FACE",FACE,{"disambiguationData":[OSD([sQuery(id+"F0.wireOp",EDGE,"E17.top")])]});
            extrude(context, id + "F28", {"entities" : qUnion([Q0]), "operationType" : NewBodyOperationType.ADD, "endBound" : BoundingType.UP_TO_SURFACE, "endBoundEntityFace" : qUnion([Q1]), "depth" : 25.4 * mm});
        }
        {
            var Q0;
            {var subQ0=sQuery(id+"F0.wireOp",EDGE,"E17.bottom");Q0=makeQuery(id+"F28.boolean.opBoolean","MERGE",FACE,{"derivedFrom":[makeQuery(id+"F1.opExtrude","CAP_FACE",FACE,{"disambiguationData":[OSD([sQuery(id+"F0.wireOp",EDGE,"E0"),sQuery(id+"F0.wireOp",EDGE,"E1"),sQuery(id+"F0.wireOp",EDGE,"E2"),sQuery(id+"F0.wireOp",EDGE,"E3"),sQuery(id+"F0.wireOp",EDGE,"E4"),sQuery(id+"F0.wireOp",EDGE,"E5"),sQuery(id+"F0.wireOp",EDGE,"E6"),sQuery(id+"F0.wireOp",EDGE,"E7"),sQuery(id+"F0.wireOp",EDGE,"E8"),sQuery(id+"F0.wireOp",EDGE,"E9"),sQuery(id+"F0.wireOp",EDGE,"E10.trimOffspring"),sQuery(id+"F0.wireOp",EDGE,"E11"),sQuery(id+"F0.wireOp",EDGE,"E12"),sQuery(id+"F0.wireOp",EDGE,"E13"),sQuery(id+"F0.wireOp",EDGE,"E14.trimOffspring"),sQuery(id+"F0.wireOp",EDGE,"E15"),sQuery(id+"F0.wireOp",EDGE,"E16"),subQ0,sQuery(id+"F0.wireOp",EDGE,"E17.top"),sQuery(id+"F0.wireOp",EDGE,"E17.left"),sQuery(id+"F0.wireOp",EDGE,"E17.right"),sQuery(id+"F0.wireOp",EDGE,"E18"),sQuery(id+"F0.wireOp",EDGE,"E20"),sQuery(id+"F0.wireOp",EDGE,"E21"),sQuery(id+"F0.wireOp",EDGE,"E22")])],"isStart":false}),makeQuery(id+"F28.opExtrude","SWEPT_FACE",FACE,{"disambiguationData":[OSD([subQ0]),TDD([makeQuery(id+"F1.opExtrude","CAP_EDGE",EDGE,{"disambiguationData":[OSD([subQ0])],"isStart":false})])]})]});}
            var sketch = newSketch(context, id + "F29", { "sketchPlane" : qUnion([Q0])});
            skLineSegment(sketch, "E101.bottom", {"start": v(-10.16, 65.24) * mm, "end": v(-6.66, 65.24) * mm});
            skLineSegment(sketch, "E101.top", {"start": v(-10.16, 62.45) * mm, "end": v(-6.66, 62.45) * mm});
            skLineSegment(sketch, "E101.left", {"start": v(-10.16, 65.24) * mm, "end": v(-10.16, 62.45) * mm});
            skLineSegment(sketch, "E101.right", {"start": v(-6.66, 65.24) * mm, "end": v(-6.66, 62.45) * mm});
            skSolve(sketch);
        }
        {
            var Q0;
            Q0 = qSketchRegion(id + "F29", true);
            extrude(context, id + "F30", {"entities" : qUnion([Q0]), "depth" : 2.1 * mm});
        }
    });
